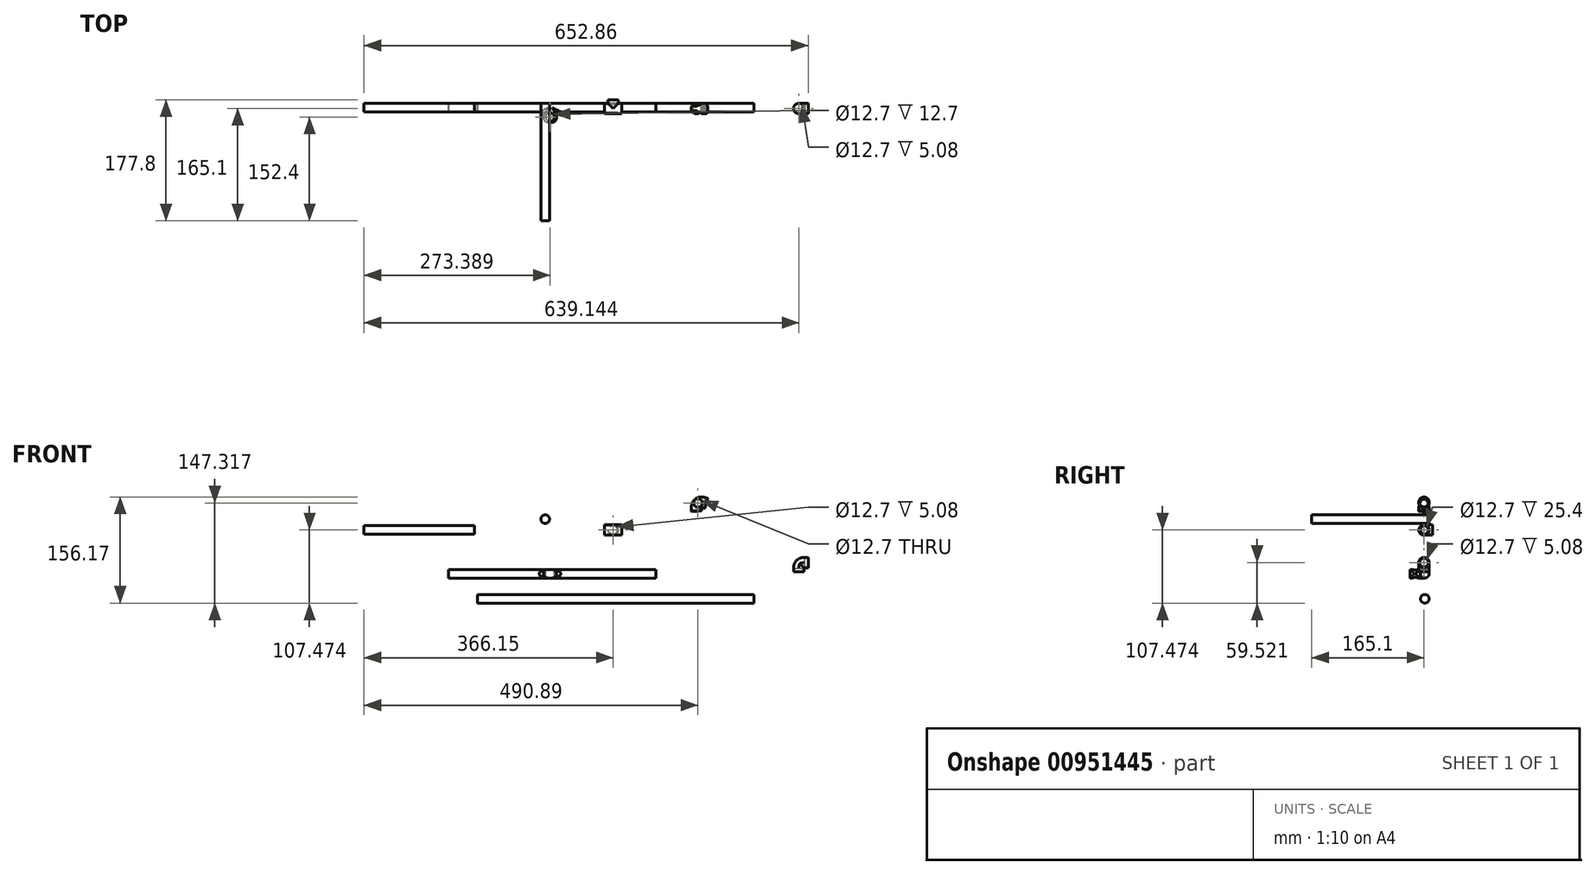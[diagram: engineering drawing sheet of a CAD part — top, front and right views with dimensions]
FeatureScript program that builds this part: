
annotation { "Feature Type Name" : "Feature", "Feature Type Description" : "" }
export const myFeature = defineFeature(function(context is Context, id is Id, definition is map)
    precondition{}
    {
        {
            var Q0;
            Q0=qCreatedBy(makeId("Front.planeOp"),FACE);
            var sketch = newSketch(context, id + "F0", { "sketchPlane" : qUnion([Q0])});
            skLineSegment(sketch, "E0.bottom", {"start": v(-378.85, 36.38) * mm, "end": v(-216.3, 36.38) * mm});
            skLineSegment(sketch, "E0.top", {"start": v(-378.85, 23.68) * mm, "end": v(-216.3, 23.68) * mm});
            skLineSegment(sketch, "E0.left", {"start": v(-378.85, 36.38) * mm, "end": v(-378.85, 23.68) * mm});
            skLineSegment(sketch, "E0.right", {"start": v(-216.3, 36.38) * mm, "end": v(-216.3, 23.68) * mm});
            skSolve(sketch);
        }
        {
            var Q0;
            Q0=makeQuery(id+"F0.imprint","IMPRINT",FACE,{"disambiguationData":[TD([[makeQuery(id+"F0.imprint","IMPRINT",EDGE,{"derivedFrom":sQuery(id+"F0.wireOp",EDGE,"E0.bottom")}),-1.0]])]});
            extrude(context, id + "F1", {"entities" : qUnion([Q0]), "depth" : 12.7 * mm, "offsetDistance" : 25.4 * mm});
        }
        {
            var Q0;
            Q0=makeQuery(id+"F1.opExtrude","CAP_EDGE",EDGE,{"disambiguationData":[OSD([sQuery(id+"F0.wireOp",EDGE,"E0.top")])],"isStart":false});
            var Q1;
            Q1=makeQuery(id+"F1.opExtrude","CAP_EDGE",EDGE,{"disambiguationData":[OSD([sQuery(id+"F0.wireOp",EDGE,"E0.top")])],"isStart":true});
            var Q2;
            Q2=makeQuery(id+"F1.opExtrude","CAP_EDGE",EDGE,{"disambiguationData":[OSD([sQuery(id+"F0.wireOp",EDGE,"E0.bottom")])],"isStart":true});
            var Q3;
            Q3=makeQuery(id+"F1.opExtrude","CAP_EDGE",EDGE,{"disambiguationData":[OSD([sQuery(id+"F0.wireOp",EDGE,"E0.bottom")])],"isStart":false});
            fillet(context, id + "F2", {"entities" : qUnion([Q0, Q1, Q2, Q3]), "radius" : 6.35 * mm, "tangentPropagation" : true, "allowEdgeOverflow" : false});
        }
        {
            var Q0;
            Q0=qCreatedBy(makeId("Front.planeOp"),FACE);
            var sketch = newSketch(context, id + "F3", { "sketchPlane" : qUnion([Q0])});
            skLineSegment(sketch, "E1.bottom", {"start": v(-254.69, -28.16) * mm, "end": v(50.11, -28.16) * mm});
            skLineSegment(sketch, "E1.top", {"start": v(-254.69, -40.86) * mm, "end": v(50.11, -40.86) * mm});
            skLineSegment(sketch, "E1.left", {"start": v(-254.69, -28.16) * mm, "end": v(-254.69, -40.86) * mm});
            skLineSegment(sketch, "E1.right", {"start": v(50.11, -28.16) * mm, "end": v(50.11, -40.86) * mm});
            skLineSegment(sketch, "E2", {"start": v(-153.09, -28.16) * mm, "end": v(-153.09, -40.86) * mm});
            skSolve(sketch);
        }
        {
            var Q0;
            Q0=makeQuery(id+"F3.imprint","IMPRINT",FACE,{"disambiguationData":[TD([[makeQuery(id+"F3.imprint","IMPRINT",EDGE,{"derivedFrom":sQuery(id+"F3.wireOp",EDGE,"E1.bottom")}),-1.0]])]});
            extrude(context, id + "F4", {"entities" : qUnion([Q0]), "depth" : 12.7 * mm, "offsetDistance" : 25.4 * mm});
        }
        {
            var Q0;
            Q0=qCreatedBy(makeId("Front.planeOp"),FACE);
            var sketch = newSketch(context, id + "F5", { "sketchPlane" : qUnion([Q0])});
            skLineSegment(sketch, "E3.bottom", {"start": v(-211.93, -65.01) * mm, "end": v(194.47, -65.01) * mm});
            skLineSegment(sketch, "E3.top", {"start": v(-211.93, -77.71) * mm, "end": v(194.47, -77.71) * mm});
            skLineSegment(sketch, "E3.left", {"start": v(-211.93, -65.01) * mm, "end": v(-211.93, -77.71) * mm});
            skLineSegment(sketch, "E3.right", {"start": v(194.47, -65.01) * mm, "end": v(194.47, -77.71) * mm});
            skSolve(sketch);
        }
        {
            var Q0;
            Q0=makeQuery(id+"F5.imprint","IMPRINT",FACE,{"disambiguationData":[TD([[makeQuery(id+"F5.imprint","IMPRINT",EDGE,{"derivedFrom":sQuery(id+"F5.wireOp",EDGE,"E3.bottom")}),-1.0]])]});
            extrude(context, id + "F6", {"entities" : qUnion([Q0]), "depth" : 12.7 * mm, "offsetDistance" : 25.4 * mm});
        }
        {
            var Q0;
            Q0=makeQuery(id+"F6.opExtrude","CAP_EDGE",EDGE,{"disambiguationData":[OSD([sQuery(id+"F5.wireOp",EDGE,"E3.top")])],"isStart":false});
            var Q1;
            Q1=makeQuery(id+"F6.opExtrude","CAP_EDGE",EDGE,{"disambiguationData":[OSD([sQuery(id+"F5.wireOp",EDGE,"E3.bottom")])],"isStart":false});
            var Q2;
            Q2=makeQuery(id+"F6.opExtrude","CAP_EDGE",EDGE,{"disambiguationData":[OSD([sQuery(id+"F5.wireOp",EDGE,"E3.bottom")])],"isStart":true});
            var Q3;
            Q3=makeQuery(id+"F6.opExtrude","CAP_EDGE",EDGE,{"disambiguationData":[OSD([sQuery(id+"F5.wireOp",EDGE,"E3.top")])],"isStart":true});
            fillet(context, id + "F7", {"entities" : qUnion([Q0, Q1, Q2, Q3]), "radius" : 6.35 * mm, "tangentPropagation" : true, "allowEdgeOverflow" : false});
        }
        {
            var Q0;
            Q0=qCreatedBy(makeId("Front.planeOp"),FACE);
            var sketch = newSketch(context, id + "F8", { "sketchPlane" : qUnion([Q0])});
            skLineSegment(sketch, "E4.top", {"start": v(252.67, -26.82) * mm, "end": v(267.91, -26.82) * mm});
            skLineSegment(sketch, "E4.left", {"start": v(252.67, -25.8) * mm, "end": v(252.67, -26.82) * mm});
            skLineSegment(sketch, "E4.right", {"start": v(267.91, -25.8) * mm, "end": v(267.91, -26.82) * mm});
            skArc(sketch, "E5", {"start": v(267.91, -10.57) * mm, "mid": v(257.14, -15.03) * mm, "end": v(252.67, -25.8) * mm});
            skLineSegment(sketch, "E6", {"start": v(267.91, -10.57) * mm, "end": v(268.93, -10.57) * mm});
            skLineSegment(sketch, "E7", {"start": v(268.93, -10.57) * mm, "end": v(268.93, -25.8) * mm});
            skLineSegment(sketch, "E8", {"start": v(268.93, -25.8) * mm, "end": v(267.91, -25.8) * mm});
            skSolve(sketch);
        }
        {
            var Q0;
            Q0=makeQuery(id+"F8.imprint","IMPRINT",FACE,{"disambiguationData":[TD([[makeQuery(id+"F8.imprint","IMPRINT",EDGE,{"derivedFrom":sQuery(id+"F8.wireOp",EDGE,"E4.top")}),1.0]])]});
            extrude(context, id + "F9", {"entities" : qUnion([Q0]), "depth" : 15.24 * mm, "offsetDistance" : 25.4 * mm});
        }
        {
            var Q0;
            Q0=makeQuery(id+"F9.opExtrude","CAP_EDGE",EDGE,{"disambiguationData":[OSD([sQuery(id+"F8.wireOp",EDGE,"E4.left")])],"isStart":false});
            var Q1;
            Q1=makeQuery(id+"F9.opExtrude","CAP_EDGE",EDGE,{"disambiguationData":[OSD([sQuery(id+"F8.wireOp",EDGE,"E4.right")])],"isStart":false});
            var Q2;
            Q2=makeQuery(id+"F9.opExtrude","CAP_EDGE",EDGE,{"disambiguationData":[OSD([sQuery(id+"F8.wireOp",EDGE,"E8")])],"isStart":false});
            var Q3;
            Q3=makeQuery(id+"F9.opExtrude","CAP_EDGE",EDGE,{"disambiguationData":[OSD([sQuery(id+"F8.wireOp",EDGE,"E4.right")])],"isStart":true});
            var Q4;
            Q4=makeQuery(id+"F9.opExtrude","CAP_EDGE",EDGE,{"disambiguationData":[OSD([sQuery(id+"F8.wireOp",EDGE,"E8")])],"isStart":true});
            var Q5;
            Q5=makeQuery(id+"F9.opExtrude","CAP_EDGE",EDGE,{"disambiguationData":[OSD([sQuery(id+"F8.wireOp",EDGE,"E5")])],"isStart":true});
            fillet(context, id + "F10", {"entities" : qUnion([Q0, Q1, Q2, Q3, Q4, Q5]), "radius" : 7.62 * mm, "tangentPropagation" : true, "allowEdgeOverflow" : false});
        }
        {
            var Q0;
            Q0=makeQuery(id+"F9.opExtrude","SWEPT_FACE",FACE,{"disambiguationData":[OSD([sQuery(id+"F8.wireOp",EDGE,"E4.top")])]});
            var sketch = newSketch(context, id + "F11", { "sketchPlane" : qUnion([Q0])});
            skCircle(sketch, "E9", {"center": v(260.3, 7.62) * mm, "radius": 6.35 * mm});
            skSolve(sketch);
        }
        {
            var Q0;
            Q0=makeQuery(id+"F9.opExtrude","SWEPT_FACE",FACE,{"disambiguationData":[OSD([sQuery(id+"F8.wireOp",EDGE,"E7")])]});
            var sketch = newSketch(context, id + "F12", { "sketchPlane" : qUnion([Q0])});
            skCircle(sketch, "E10", {"center": v(-7.62, -18.19) * mm, "radius": 6.35 * mm});
            skSolve(sketch);
        }
        {
            var Q0;
            Q0=makeQuery(id+"F11.imprint","IMPRINT",FACE,{"disambiguationData":[TD([[makeQuery(id+"F11.imprint","IMPRINT",EDGE,{"derivedFrom":sQuery(id+"F11.wireOp",EDGE,"E9")}),-1.0]])]});
            extrude(context, id + "F13", {"entities" : qUnion([Q0]), "operationType" : NewBodyOperationType.ADD, "depth" : 5.08 * mm, "offsetDistance" : 25.4 * mm});
        }
        {
            var Q0;
            Q0=makeQuery(id+"F12.imprint","IMPRINT",FACE,{"disambiguationData":[TD([[makeQuery(id+"F12.imprint","IMPRINT",EDGE,{"derivedFrom":sQuery(id+"F12.wireOp",EDGE,"E10")}),-1.0]])]});
            extrude(context, id + "F14", {"entities" : qUnion([Q0]), "operationType" : NewBodyOperationType.ADD, "depth" : 5.08 * mm, "offsetDistance" : 25.4 * mm});
        }
        {
            var Q0;
            Q0=qCreatedBy(makeId("Front.planeOp"),FACE);
            var sketch = newSketch(context, id + "F15", { "sketchPlane" : qUnion([Q0])});
            skLineSegment(sketch, "E11.bottom", {"start": v(-25.4, 37.38) * mm, "end": v(0, 37.38) * mm});
            skLineSegment(sketch, "E11.top", {"start": v(-25.4, 22.14) * mm, "end": v(0, 22.14) * mm});
            skLineSegment(sketch, "E11.left", {"start": v(-25.4, 37.38) * mm, "end": v(-25.4, 22.14) * mm});
            skLineSegment(sketch, "E11.right", {"start": v(0, 37.38) * mm, "end": v(0, 22.14) * mm});
            skSolve(sketch);
        }
        {
            var Q0;
            Q0=makeQuery(id+"F15.imprint","IMPRINT",FACE,{"disambiguationData":[TD([[makeQuery(id+"F15.imprint","IMPRINT",EDGE,{"derivedFrom":sQuery(id+"F15.wireOp",EDGE,"E11.bottom")}),-1.0]])]});
            extrude(context, id + "F16", {"entities" : qUnion([Q0]), "depth" : 15.24 * mm, "offsetDistance" : 25.4 * mm});
        }
        {
            var Q0;
            Q0=makeQuery(id+"F16.opExtrude","SWEPT_FACE",FACE,{"disambiguationData":[OSD([sQuery(id+"F15.wireOp",EDGE,"E11.right")])]});
            var sketch = newSketch(context, id + "F17", { "sketchPlane" : qUnion([Q0])});
            skPoint(sketch, "E12", {"position": v(-7.62, 29.76) * mm});
            skSolve(sketch);
        }
        {
            var Q0;
            Q0=sQuery(id+"F17.wireOp",VERTEX,"E12");
            var Q1;
            Q1=makeQuery(id+"F16.opExtrude","SWEPT_BODY",BODY,{"disambiguationData":[OSD([sQuery(id+"F15.wireOp",EDGE,"E11.bottom"),sQuery(id+"F15.wireOp",EDGE,"E11.top"),sQuery(id+"F15.wireOp",EDGE,"E11.left"),sQuery(id+"F15.wireOp",EDGE,"E11.right")])]});
            hole(context, id + "F18", {"style" : HoleStyle.SIMPLE, "endStyle" : HoleEndStyle.THROUGH, "holeDiameter" : 12.7 * mm, "majorDiameter" : 6.35 * mm, "isTappedThrough" : true, "tappedDepth" : 12.7 * mm, "tapClearance" : 3, "locations" : qUnion([Q0]), "scope" : qUnion([Q1])});
        }
        {
            var Q0;
            Q0=makeQuery(id+"F16.opExtrude","CAP_FACE",FACE,{"disambiguationData":[OSD([sQuery(id+"F15.wireOp",EDGE,"E11.bottom"),sQuery(id+"F15.wireOp",EDGE,"E11.top"),sQuery(id+"F15.wireOp",EDGE,"E11.left"),sQuery(id+"F15.wireOp",EDGE,"E11.right")])],"isStart":true});
            var sketch = newSketch(context, id + "F19", { "sketchPlane" : qUnion([Q0])});
            skLineSegment(sketch, "E13", {"start": v(12.7, 37.38) * mm, "end": v(12.7, 22.14) * mm, "construction": true});
            skLineSegment(sketch, "E14.bottom", {"start": v(20.32, 22.14) * mm, "end": v(5.08, 22.14) * mm});
            skLineSegment(sketch, "E14.top", {"start": v(20.32, 37.38) * mm, "end": v(5.08, 37.38) * mm});
            skLineSegment(sketch, "E14.left", {"start": v(20.32, 22.14) * mm, "end": v(20.32, 37.38) * mm});
            skLineSegment(sketch, "E14.right", {"start": v(5.08, 22.14) * mm, "end": v(5.08, 37.38) * mm});
            skPoint(sketch, "E14.middle", {"position": v(12.7, 29.76) * mm});
            skCircle(sketch, "E15", {"center": v(12.7, 29.76) * mm, "radius": 6.35 * mm});
            skSolve(sketch);
        }
        {
            var Q0;
            Q0=makeQuery(id+"F19.imprint","IMPRINT",FACE,{"disambiguationData":[TD([[makeQuery(id+"F19.imprint","IMPRINT",EDGE,{"derivedFrom":sQuery(id+"F19.wireOp",EDGE,"E14.bottom")}),-1.0]])]});
            extrude(context, id + "F20", {"entities" : qUnion([Q0]), "operationType" : NewBodyOperationType.ADD, "depth" : 5.08 * mm, "offsetDistance" : 25.4 * mm});
        }
        {
            var Q0;
            {var subQ0=sQuery(id+"F15.wireOp",EDGE,"E11.right");var subQ1=sQuery(id+"F15.wireOp",EDGE,"E11.bottom");Q0=makeQuery(id+"F20.boolean.opBoolean","SPLIT",EDGE,{"disambiguationData":[TD([makeQuery(id+"F16.opExtrude","SWEPT_FACE",FACE,{"disambiguationData":[OSD([subQ0])]})])],"derivedFrom":makeQuery(id+"F16.opExtrude","CAP_EDGE",EDGE,{"disambiguationData":[OSD([subQ1])],"isStart":true})});}
            var Q1;
            Q1=makeQuery(id+"F20.opExtrude","SWEPT_EDGE",EDGE,{"disambiguationData":[OSD([sQuery(id+"F15.wireOp",EDGE,"E11.bottom"),sQuery(id+"F19.wireOp",EDGE,"E14.top"),sQuery(id+"F19.wireOp",EDGE,"E14.right")])]});
            var Q2;
            Q2=makeQuery(id+"F16.opExtrude","CAP_EDGE",EDGE,{"disambiguationData":[OSD([sQuery(id+"F15.wireOp",EDGE,"E11.bottom")])],"isStart":false});
            var Q3;
            {var subQ0=sQuery(id+"F15.wireOp",EDGE,"E11.right");var subQ1=sQuery(id+"F15.wireOp",EDGE,"E11.top");Q3=makeQuery(id+"F20.boolean.opBoolean","SPLIT",EDGE,{"disambiguationData":[TD([makeQuery(id+"F16.opExtrude","SWEPT_FACE",FACE,{"disambiguationData":[OSD([subQ0])]})])],"derivedFrom":makeQuery(id+"F16.opExtrude","CAP_EDGE",EDGE,{"disambiguationData":[OSD([subQ1])],"isStart":true})});}
            var Q4;
            Q4=makeQuery(id+"F20.opExtrude","SWEPT_EDGE",EDGE,{"disambiguationData":[OSD([sQuery(id+"F15.wireOp",EDGE,"E11.top"),sQuery(id+"F19.wireOp",EDGE,"E14.bottom"),sQuery(id+"F19.wireOp",EDGE,"E14.right")])]});
            var Q5;
            Q5=makeQuery(id+"F20.opExtrude","SWEPT_EDGE",EDGE,{"disambiguationData":[OSD([sQuery(id+"F15.wireOp",EDGE,"E11.bottom"),sQuery(id+"F19.wireOp",EDGE,"E14.top"),sQuery(id+"F19.wireOp",EDGE,"E14.left")])]});
            var Q6;
            {var subQ0=sQuery(id+"F15.wireOp",EDGE,"E11.left");var subQ1=sQuery(id+"F15.wireOp",EDGE,"E11.bottom");Q6=makeQuery(id+"F20.boolean.opBoolean","SPLIT",EDGE,{"disambiguationData":[TD([makeQuery(id+"F16.opExtrude","SWEPT_FACE",FACE,{"disambiguationData":[OSD([subQ0])]})])],"derivedFrom":makeQuery(id+"F16.opExtrude","CAP_EDGE",EDGE,{"disambiguationData":[OSD([subQ1])],"isStart":true})});}
            var Q7;
            Q7=makeQuery(id+"F16.opExtrude","CAP_EDGE",EDGE,{"disambiguationData":[OSD([sQuery(id+"F15.wireOp",EDGE,"E11.top")])],"isStart":false});
            var Q8;
            {var subQ0=sQuery(id+"F15.wireOp",EDGE,"E11.left");var subQ1=sQuery(id+"F15.wireOp",EDGE,"E11.top");Q8=makeQuery(id+"F20.boolean.opBoolean","SPLIT",EDGE,{"disambiguationData":[TD([makeQuery(id+"F16.opExtrude","SWEPT_FACE",FACE,{"disambiguationData":[OSD([subQ0])]})])],"derivedFrom":makeQuery(id+"F16.opExtrude","CAP_EDGE",EDGE,{"disambiguationData":[OSD([subQ1])],"isStart":true})});}
            var Q9;
            Q9=makeQuery(id+"F20.opExtrude","SWEPT_EDGE",EDGE,{"disambiguationData":[OSD([sQuery(id+"F15.wireOp",EDGE,"E11.top"),sQuery(id+"F19.wireOp",EDGE,"E14.bottom"),sQuery(id+"F19.wireOp",EDGE,"E14.left")])]});
            fillet(context, id + "F21", {"entities" : qUnion([Q0, Q1, Q2, Q3, Q4, Q5, Q6, Q7, Q8, Q9]), "radius" : 7.62 * mm, "tangentPropagation" : true, "allowEdgeOverflow" : false});
        }
        {
            var Q0;
            Q0=makeQuery(id+"F4.opExtrude","CAP_FACE",FACE,{"disambiguationData":[OSD([sQuery(id+"F3.wireOp",EDGE,"E1.bottom"),sQuery(id+"F3.wireOp",EDGE,"E1.top"),sQuery(id+"F3.wireOp",EDGE,"E1.left"),sQuery(id+"F3.wireOp",EDGE,"E1.right")])],"isStart":false});
            var sketch = newSketch(context, id + "F22", { "sketchPlane" : qUnion([Q0])});
            skPoint(sketch, "E16", {"position": v(-105.46, -34.51) * mm});
            skLineSegment(sketch, "E17.bottom", {"start": v(-95.94, -40.86) * mm, "end": v(-114.99, -40.86) * mm});
            skLineSegment(sketch, "E17.top", {"start": v(-95.94, -28.16) * mm, "end": v(-114.99, -28.16) * mm});
            skLineSegment(sketch, "E17.left", {"start": v(-95.94, -40.86) * mm, "end": v(-95.94, -28.16) * mm});
            skLineSegment(sketch, "E17.right", {"start": v(-114.99, -40.86) * mm, "end": v(-114.99, -28.16) * mm});
            skSolve(sketch);
        }
        {
            var Q0;
            Q0=makeQuery(id+"F22.imprint","IMPRINT",FACE,{"disambiguationData":[TD([[makeQuery(id+"F22.imprint","IMPRINT",EDGE,{"derivedFrom":sQuery(id+"F22.wireOp",EDGE,"E17.bottom")}),1.0]])]});
            extrude(context, id + "F23", {"entities" : qUnion([Q0]), "operationType" : NewBodyOperationType.ADD, "depth" : 15.24 * mm, "offsetDistance" : 25.4 * mm});
        }
        {
            var Q0;
            Q0=makeQuery(id+"F23.boolean.opBoolean","MERGE",FACE,{"derivedFrom":[makeQuery(id+"F4.opExtrude","SWEPT_FACE",FACE,{"disambiguationData":[OSD([sQuery(id+"F3.wireOp",EDGE,"E1.bottom")])]}),makeQuery(id+"F23.opExtrude","SWEPT_FACE",FACE,{"disambiguationData":[OSD([sQuery(id+"F22.wireOp",EDGE,"E17.top")])]})]});
            var sketch = newSketch(context, id + "F24", { "sketchPlane" : qUnion([Q0])});
            skLineSegment(sketch, "E18", {"start": v(-114.99, -12.7) * mm, "end": v(-95.94, -12.7) * mm, "construction": true});
            skLineSegment(sketch, "E19", {"start": v(-105.46, -12.7) * mm, "end": v(-105.46, -27.94) * mm, "construction": true});
            skLineSegment(sketch, "E20", {"start": v(-114.99, -20.32) * mm, "end": v(-95.94, -20.32) * mm, "construction": true});
            skCircle(sketch, "E21", {"center": v(-105.46, -20.32) * mm, "radius": 6.35 * mm});
            skSolve(sketch);
        }
        {
            var Q0;
            Q0=sQuery(id+"F24.wireOp",VERTEX,"E21.center");
            var Q1;
            Q1=makeQuery(id+"F4.opExtrude","SWEPT_BODY",BODY,{"disambiguationData":[OSD([sQuery(id+"F3.wireOp",EDGE,"E1.bottom"),sQuery(id+"F3.wireOp",EDGE,"E1.top"),sQuery(id+"F3.wireOp",EDGE,"E1.left"),sQuery(id+"F3.wireOp",EDGE,"E1.right")])]});
            hole(context, id + "F25", {"style" : HoleStyle.SIMPLE, "endStyle" : HoleEndStyle.THROUGH, "holeDiameter" : 12.7 * mm, "majorDiameter" : 6.35 * mm, "isTappedThrough" : true, "tappedDepth" : 12.7 * mm, "tapClearance" : 3, "locations" : qUnion([Q0]), "scope" : qUnion([Q1])});
        }
        {
            var Q0;
            {var subQ0=sQuery(id+"F3.wireOp",EDGE,"E1.left");var subQ1=sQuery(id+"F3.wireOp",EDGE,"E1.bottom");Q0=makeQuery(id+"F23.boolean.opBoolean","SPLIT",EDGE,{"disambiguationData":[TD([makeQuery(id+"F4.opExtrude","SWEPT_FACE",FACE,{"disambiguationData":[OSD([subQ0])]})])],"derivedFrom":makeQuery(id+"F4.opExtrude","CAP_EDGE",EDGE,{"disambiguationData":[OSD([subQ1])],"isStart":false})});}
            var Q1;
            {var subQ0=sQuery(id+"F3.wireOp",EDGE,"E1.right");var subQ1=sQuery(id+"F3.wireOp",EDGE,"E1.bottom");Q1=makeQuery(id+"F23.boolean.opBoolean","SPLIT",EDGE,{"disambiguationData":[TD([makeQuery(id+"F4.opExtrude","SWEPT_FACE",FACE,{"disambiguationData":[OSD([subQ0])]})])],"derivedFrom":makeQuery(id+"F4.opExtrude","CAP_EDGE",EDGE,{"disambiguationData":[OSD([subQ1])],"isStart":false})});}
            var Q2;
            Q2=makeQuery(id+"F4.opExtrude","CAP_EDGE",EDGE,{"disambiguationData":[OSD([sQuery(id+"F3.wireOp",EDGE,"E1.bottom")])],"isStart":true});
            var Q3;
            Q3=makeQuery(id+"F4.opExtrude","CAP_EDGE",EDGE,{"disambiguationData":[OSD([sQuery(id+"F3.wireOp",EDGE,"E1.top")])],"isStart":true});
            var Q4;
            {var subQ0=sQuery(id+"F3.wireOp",EDGE,"E1.left");var subQ1=sQuery(id+"F3.wireOp",EDGE,"E1.top");Q4=makeQuery(id+"F23.boolean.opBoolean","SPLIT",EDGE,{"disambiguationData":[TD([makeQuery(id+"F4.opExtrude","SWEPT_FACE",FACE,{"disambiguationData":[OSD([subQ0])]})])],"derivedFrom":makeQuery(id+"F4.opExtrude","CAP_EDGE",EDGE,{"disambiguationData":[OSD([subQ1])],"isStart":false})});}
            var Q5;
            {var subQ0=sQuery(id+"F3.wireOp",EDGE,"E1.right");var subQ1=sQuery(id+"F3.wireOp",EDGE,"E1.top");Q5=makeQuery(id+"F23.boolean.opBoolean","SPLIT",EDGE,{"disambiguationData":[TD([makeQuery(id+"F4.opExtrude","SWEPT_FACE",FACE,{"disambiguationData":[OSD([subQ0])]})])],"derivedFrom":makeQuery(id+"F4.opExtrude","CAP_EDGE",EDGE,{"disambiguationData":[OSD([subQ1])],"isStart":false})});}
            fillet(context, id + "F26", {"entities" : qUnion([Q0, Q1, Q2, Q3, Q4, Q5]), "radius" : 6.35 * mm, "tangentPropagation" : true, "allowEdgeOverflow" : false});
        }
        {
            var Q0;
            Q0=makeQuery(id+"F23.opExtrude","CAP_EDGE",EDGE,{"disambiguationData":[OSD([sQuery(id+"F22.wireOp",EDGE,"E17.right")])],"isStart":false});
            var Q1;
            Q1=makeQuery(id+"F23.opExtrude","CAP_EDGE",EDGE,{"disambiguationData":[OSD([sQuery(id+"F22.wireOp",EDGE,"E17.left")])],"isStart":false});
            var Q2;
            Q2=makeQuery(id+"F23.opExtrude","SWEPT_EDGE",EDGE,{"disambiguationData":[OSD([sQuery(id+"F3.wireOp",EDGE,"E1.bottom"),sQuery(id+"F22.wireOp",EDGE,"E17.top"),sQuery(id+"F22.wireOp",EDGE,"E17.right")])]});
            var Q3;
            Q3=makeQuery(id+"F23.opExtrude","SWEPT_EDGE",EDGE,{"disambiguationData":[OSD([sQuery(id+"F3.wireOp",EDGE,"E1.bottom"),sQuery(id+"F22.wireOp",EDGE,"E17.top"),sQuery(id+"F22.wireOp",EDGE,"E17.left")])]});
            var Q4;
            Q4=makeQuery(id+"F23.opExtrude","SWEPT_FACE",FACE,{"disambiguationData":[OSD([sQuery(id+"F22.wireOp",EDGE,"E17.right")])]});
            var Q5;
            Q5=makeQuery(id+"F23.opExtrude","SWEPT_EDGE",EDGE,{"disambiguationData":[OSD([sQuery(id+"F3.wireOp",EDGE,"E1.top"),sQuery(id+"F22.wireOp",EDGE,"E17.bottom"),sQuery(id+"F22.wireOp",EDGE,"E17.left")])]});
            var Q6;
            {var subQ0=makeQuery(id+"F23.opExtrude","SWEPT_FACE",FACE,{"disambiguationData":[OSD([sQuery(id+"F22.wireOp",EDGE,"E17.left")])]});var subQ1=sQuery(id+"F3.wireOp",EDGE,"E1.right");var subQ2=sQuery(id+"F3.wireOp",EDGE,"E1.bottom");Q6=makeQuery(id+"F26.opFillet","BLEND_EDGE",EDGE,{"blendedFrom":[makeQuery(id+"F23.boolean.opBoolean","SPLIT",EDGE,{"disambiguationData":[TD([makeQuery(id+"F4.opExtrude","SWEPT_FACE",FACE,{"disambiguationData":[OSD([subQ1])]})])],"derivedFrom":makeQuery(id+"F4.opExtrude","CAP_EDGE",EDGE,{"disambiguationData":[OSD([subQ2])],"isStart":false})}),subQ0],"blendedInto":[subQ0]});}
            fillet(context, id + "F27", {"entities" : qUnion([Q0, Q1, Q2, Q3, Q4, Q5, Q6]), "radius" : 6.35 * mm, "tangentPropagation" : true, "allowEdgeOverflow" : false});
        }
        {
            var Q0;
            Q0=qCreatedBy(makeId("Front.planeOp"),FACE);
            var sketch = newSketch(context, id + "F28", { "sketchPlane" : qUnion([Q0])});
            skLineSegment(sketch, "E22", {"start": v(117.55, 60.68) * mm, "end": v(117.34, 63.22) * mm});
            skLineSegment(sketch, "E23", {"start": v(117.34, 63.22) * mm, "end": v(119.8, 62.54) * mm});
            skLineSegment(sketch, "E24", {"start": v(117.55, 60.68) * mm, "end": v(102.36, 59.44) * mm});
            skLineSegment(sketch, "E25", {"start": v(102.36, 59.44) * mm, "end": v(102.15, 61.98) * mm});
            skLineSegment(sketch, "E26", {"start": v(102.15, 61.98) * mm, "end": v(117.34, 63.22) * mm});
            skLineSegment(sketch, "E27", {"start": v(119.8, 62.54) * mm, "end": v(123.82, 77.24) * mm});
            skLineSegment(sketch, "E28", {"start": v(123.82, 77.24) * mm, "end": v(121.37, 77.91) * mm});
            skLineSegment(sketch, "E29", {"start": v(121.37, 77.91) * mm, "end": v(117.34, 63.22) * mm});
            skArc(sketch, "E30", {"start": v(123.76, 77.04) * mm, "mid": v(107.61, 74.95) * mm, "end": v(102.57, 59.46) * mm});
            skSolve(sketch);
        }
        {
            var Q0;
            {var subQ0=sQuery(id+"F28.wireOp",EDGE,"E22");Q0=makeQuery(id+"F28.imprint","IMPRINT",FACE,{"disambiguationData":[TD([[makeQuery(id+"F28.imprint","IMPRINT",EDGE,{"derivedFrom":subQ0}),1.0]])]});}
            var Q1;
            {var subQ0=sQuery(id+"F28.wireOp",EDGE,"E26");Q1=makeQuery(id+"F28.imprint","IMPRINT",FACE,{"disambiguationData":[TD([[makeQuery(id+"F28.imprint","IMPRINT",EDGE,{"derivedFrom":subQ0}),1.0]])]});}
            var Q2;
            {var subQ0=sQuery(id+"F28.wireOp",EDGE,"E23");Q2=makeQuery(id+"F28.imprint","IMPRINT",FACE,{"disambiguationData":[TD([[makeQuery(id+"F28.imprint","IMPRINT",EDGE,{"derivedFrom":subQ0}),1.0]])]});}
            var Q3;
            {var subQ0=sQuery(id+"F28.wireOp",EDGE,"E28");Q3=makeQuery(id+"F28.imprint","IMPRINT",FACE,{"disambiguationData":[TD([[makeQuery(id+"F28.imprint","IMPRINT",EDGE,{"derivedFrom":subQ0}),1.0]])]});}
            var Q4;
            {var subQ0=sQuery(id+"F28.wireOp",EDGE,"E25");Q4=makeQuery(id+"F28.imprint","IMPRINT",FACE,{"disambiguationData":[TD([[makeQuery(id+"F28.imprint","IMPRINT",EDGE,{"derivedFrom":subQ0}),-1.0]])]});}
            extrude(context, id + "F29", {"entities" : qUnion([Q0, Q1, Q2, Q3, Q4]), "depth" : 15.24 * mm, "offsetDistance" : 25.4 * mm});
        }
        {
            var Q0;
            Q0=makeQuery(id+"F29.opExtrude","CAP_FACE",FACE,{"disambiguationData":[OSD([sQuery(id+"F28.wireOp",EDGE,"E22"),sQuery(id+"F28.wireOp",EDGE,"E23"),sQuery(id+"F28.wireOp",EDGE,"E24"),sQuery(id+"F28.wireOp",EDGE,"E25"),sQuery(id+"F28.wireOp",EDGE,"E27"),sQuery(id+"F28.wireOp",EDGE,"E28"),sQuery(id+"F28.wireOp",EDGE,"E30")])],"isStart":true});
            var sketch = newSketch(context, id + "F30", { "sketchPlane" : qUnion([Q0])});
            skLineSegment(sketch, "E31", {"start": v(-117.34, 63.22) * mm, "end": v(-107.61, 74.95) * mm, "construction": true});
            skPoint(sketch, "E32", {"position": v(-112.04, 69.6) * mm});
            skSolve(sketch);
        }
        {
            var Q0;
            Q0=sQuery(id+"F30.wireOp",VERTEX,"E32");
            var Q1;
            Q1=makeQuery(id+"F29.opExtrude","SWEPT_BODY",BODY,{"disambiguationData":[OSD([sQuery(id+"F28.wireOp",EDGE,"E22"),sQuery(id+"F28.wireOp",EDGE,"E23"),sQuery(id+"F28.wireOp",EDGE,"E24"),sQuery(id+"F28.wireOp",EDGE,"E25"),sQuery(id+"F28.wireOp",EDGE,"E27"),sQuery(id+"F28.wireOp",EDGE,"E28"),sQuery(id+"F28.wireOp",EDGE,"E30")])]});
            hole(context, id + "F31", {"style" : HoleStyle.SIMPLE, "endStyle" : HoleEndStyle.THROUGH, "holeDiameter" : 12.7 * mm, "majorDiameter" : 6.35 * mm, "isTappedThrough" : true, "tappedDepth" : 12.7 * mm, "tapClearance" : 3, "locations" : qUnion([Q0]), "scope" : qUnion([Q1])});
        }
        {
            var Q0;
            Q0=makeQuery(id+"F29.opExtrude","CAP_EDGE",EDGE,{"disambiguationData":[OSD([sQuery(id+"F28.wireOp",EDGE,"E30")])],"isStart":false});
            var Q1;
            Q1=makeQuery(id+"F29.opExtrude","CAP_EDGE",EDGE,{"disambiguationData":[OSD([sQuery(id+"F28.wireOp",EDGE,"E30")])],"isStart":true});
            var Q2;
            Q2=makeQuery(id+"F29.opExtrude","CAP_EDGE",EDGE,{"disambiguationData":[OSD([sQuery(id+"F28.wireOp",EDGE,"E23")])],"isStart":true});
            var Q3;
            Q3=makeQuery(id+"F29.opExtrude","CAP_EDGE",EDGE,{"disambiguationData":[OSD([sQuery(id+"F28.wireOp",EDGE,"E23")])],"isStart":false});
            fillet(context, id + "F32", {"entities" : qUnion([Q0, Q1, Q2, Q3]), "radius" : 7.62 * mm, "tangentPropagation" : true, "allowEdgeOverflow" : false});
        }
        {
            var Q0;
            Q0=makeQuery(id+"F29.opExtrude","CAP_EDGE",EDGE,{"disambiguationData":[OSD([sQuery(id+"F28.wireOp",EDGE,"E22")])],"isStart":true});
            var Q1;
            Q1=makeQuery(id+"F29.opExtrude","CAP_EDGE",EDGE,{"disambiguationData":[OSD([sQuery(id+"F28.wireOp",EDGE,"E22")])],"isStart":false});
            fillet(context, id + "F33", {"entities" : qUnion([Q0, Q1]), "radius" : 7.62 * mm, "tangentPropagation" : true, "allowEdgeOverflow" : false});
        }
        {
            var Q0;
            Q0=makeQuery(id+"F29.opExtrude","SWEPT_FACE",FACE,{"disambiguationData":[OSD([sQuery(id+"F28.wireOp",EDGE,"E24")])]});
            var sketch = newSketch(context, id + "F34", { "sketchPlane" : qUnion([Q0])});
            skCircle(sketch, "E33", {"center": v(114.48, 7.62) * mm, "radius": 6.35 * mm});
            skSolve(sketch);
        }
        {
            var Q0;
            Q0=makeQuery(id+"F29.opExtrude","SWEPT_FACE",FACE,{"disambiguationData":[OSD([sQuery(id+"F28.wireOp",EDGE,"E27")])]});
            var sketch = newSketch(context, id + "F35", { "sketchPlane" : qUnion([Q0])});
            skCircle(sketch, "E34", {"center": v(-7.62, 99.61) * mm, "radius": 6.35 * mm});
            skSolve(sketch);
        }
        {
            var Q0;
            Q0=makeQuery(id+"F35.imprint","IMPRINT",FACE,{"disambiguationData":[TD([[makeQuery(id+"F35.imprint","IMPRINT",EDGE,{"derivedFrom":sQuery(id+"F35.wireOp",EDGE,"E34")}),-1.0]])]});
            extrude(context, id + "F36", {"entities" : qUnion([Q0]), "operationType" : NewBodyOperationType.ADD, "depth" : 2.54 * mm, "offsetDistance" : 25.4 * mm});
        }
        {
            var Q0;
            Q0=makeQuery(id+"F34.imprint","IMPRINT",FACE,{"disambiguationData":[TD([[makeQuery(id+"F34.imprint","IMPRINT",EDGE,{"derivedFrom":sQuery(id+"F34.wireOp",EDGE,"E33")}),-1.0]])]});
            extrude(context, id + "F37", {"entities" : qUnion([Q0]), "operationType" : NewBodyOperationType.ADD, "depth" : 2.54 * mm, "offsetDistance" : 25.4 * mm});
        }
        {
            var Q0;
            Q0=qCreatedBy(makeId("Front.planeOp"),FACE);
            var sketch = newSketch(context, id + "F38", { "sketchPlane" : qUnion([Q0])});
            skCircle(sketch, "E35", {"center": v(-112.56, 45.72) * mm, "radius": 6.35 * mm});
            skSolve(sketch);
        }
        {
            var Q0;
            Q0=makeQuery(id+"F38.imprint","IMPRINT",FACE,{"disambiguationData":[TD([[makeQuery(id+"F38.imprint","IMPRINT",EDGE,{"derivedFrom":sQuery(id+"F38.wireOp",EDGE,"E35")}),1.0]])]});
            extrude(context, id + "F39", {"entities" : qUnion([Q0]), "depth" : 172.72 * mm, "offsetDistance" : 25.4 * mm});
        }
    });
